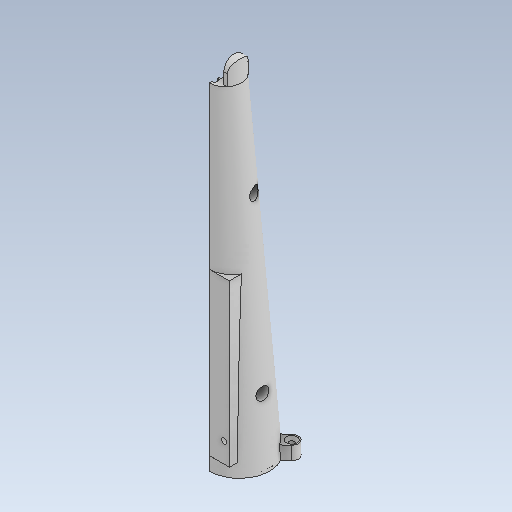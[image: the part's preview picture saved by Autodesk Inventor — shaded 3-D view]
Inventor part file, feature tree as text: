
AUTODESK INVENTOR PART (.ipt)
format: ipt  version: 2021 (Build 250183000, 183)  size: 1,106,432 bytes
history: native  units: mm
features: sketch x40, extrude x38, plane x17, fillet x9, hole x3, thread x3, loft x2, revolve x2, other x1
ambient origin geometry x8: Origin, YZ Plane, XZ Plane, XY Plane, X Axis, Y Axis, Z Axis, Center Point
bodies: Body1 (feature_tree)
feature tree (115):
  other  "Sólido1"
  plane  "Plano de trabajo1"
  plane  "Plano de trabajo2"
  plane  "Plano de trabajo4"
  plane  "Plano de trabajo5"
  plane  "Plano de trabajo6"
  sketch  "Boceto1"  dims[d1=250.0mm d2=0.0mm d3=-80.0mm d4=-110.0mm]
  sketch  "Boceto2"  dims[d5=-140.0mm d7=-0.0mm d8=2.0mm]
  sketch  "Boceto3"  dims[d9=140.0mm d10=250.0mm]
  sketch  "Boceto4"  dims[d11=24.0mm d22=0.0mm d23=90.0deg d24=0.0mm d25=90.0deg]
  sketch  "Boceto6"  dims[d44=45.0mm d49=29.11157mm]
  sketch  "Boceto7"  dims[d50=29.11157mm d53=29.11157mm]
  loft  "Solevación1"
  fillet  "Empalme2"  [1 undecoded]
  extrude  "Extrusión1"  TaperAngle=0.0deg  [1 undecoded]
  fillet  "Empalme5"  Radius=2.0mm
  plane  "Plano de trabajo7"
  extrude  "Extrusión2"  Depth=250.0mm
  plane  "Plano de trabajo8"
  plane  "Plano de trabajo9"
  loft  "Solevación9"
  plane  "Plano de trabajo10"
  extrude  "Extrusión3"  Depth=29.11157mm
  plane  "Plano de trabajo11"
  revolve  "Revolución1"  [1 undecoded]
  revolve  "Revolución2"  [1 undecoded]
  extrude  "Extrusión4"  Depth=32.5mm
  plane  "Plano de trabajo12"
  extrude  "Extrusión5"  Depth=44.747934mm
  plane  "Plano de trabajo13"
  plane  "Plano de trabajo14"
  extrude  "Extrusión6"  Depth=42.747934mm
  extrude  "Extrusión7"  Depth=42.747934mm
  extrude  "Extrusión8"  Depth=13.0mm
  extrude  "Extrusión11"  Depth=6.5mm
  extrude  "Extrusión9"  Depth=7.75mm
  extrude  "Extrusión10"  Depth=16.0mm
  extrude  "Extrusión12"  Depth=12.0mm
  sketch  "Boceto30"  dims[d160=-19.75mm d161=0.0mm]
  extrude  "Extrusión13"  Depth=7.75mm
  extrude  "Extrusión14"  Depth=6.5mm
  extrude  "Extrusión15"  TaperAngle=0.0deg  [1 undecoded]
  hole  "Agujero1"  [1 undecoded]
  thread  "Rosca1"  [1 undecoded]
  extrude  "Extrusión16"  Depth=2.0mm
  plane  "Plano de trabajo16"
  extrude  "Extrusión17"  TaperAngle=0.0deg  [1 undecoded]
  extrude  "Extrusión18"  TaperAngle=0.0deg  [1 undecoded]
  plane  "Plano de trabajo17"
  sketch  "Boceto46"  dims[d185=2.0mm d187=1.0mm]
  hole  "Agujero2"  [1 undecoded]
  hole  "Agujero3"  [1 undecoded]
  plane  "Plano de trabajo19"
  sketch  "Boceto50"  dims[d193=0.25mm d194=90.0deg]
  extrude  "Extrusión22"  Depth=12.0mm
  extrude  "Extrusión23"  [1 undecoded]
  extrude  "Extrusión24"  Depth=0.75mm
  plane  "Plano de trabajo20"
  extrude  "Extrusión25"  Depth=1.0mm
  fillet  "Empalme6"  Radius=11.0mm
  fillet  "Empalme7"  Radius=17.453293mm
  sketch  "Boceto49"  dims[d191=2.0mm d192=0.25mm]
  extrude  "Extrusión29"  Depth=0.75mm
  extrude  "Extrusión30"  Depth=0.25mm
  sketch  "Boceto44"  dims[d181=0.75mm d182=0.25mm]
  sketch  "Boceto47"  dims[d189=3.0mm d190=2.0mm]
  extrude  "Extrusión26"  Depth=0.25mm
  extrude  "Extrusión27"  Depth=2.0mm
  extrude  "Extrusión28"  Depth=2.0mm
  sketch  "Boceto45"  dims[d183=1.0mm d184=0.25mm]
  extrude  "Extrusión31"  Depth=2.0mm
  extrude  "Extrusión32"  TaperAngle=90.0deg  [1 undecoded]
  extrude  "Extrusión33"  [1 undecoded]
  extrude  "Extrusión34"  Depth=20.0mm
  extrude  "Extrusión35"  Depth=2.0mm
  thread  "Rosca2"  [1 undecoded]
  thread  "Rosca3"  [1 undecoded]
  fillet  "Empalme8"  [1 undecoded]
  fillet  "Empalme9"  Radius=0.5mm
  fillet  "Empalme10"  Radius=0.25mm
  fillet  "Empalme11"  [1 undecoded]
  extrude  "Extrusión36"  Depth=1.8mm TaperAngle=0.0deg
  extrude  "Extrusión37"  Depth=1.8mm TaperAngle=0.0deg
  fillet  "Empalme12"  Radius=2.0mm
  sketch  "Boceto54"  dims[d201=9.0mm d202=9.0mm d203=2.0mm d204=201.65mm d205=0.0mm d206=0.5mm d207=0.25mm d208=-7.5mm]
  extrude  "Agujero_tornillo_caja"  Depth=1.8mm
  extrude  "Extrusión40"  Depth=6.5mm
  extrude  "Test_section"  Depth=1.8mm
  extrude  "Extrusión41"  Depth=1.8mm
  sketch  "Boceto55"  dims[d209=100.0mm d210=0.0mm d211=35.0mm d212=0.0mm d213=210.0mm d214=0.0mm d215=2.0mm d216=1.059493mm d217=6.5mm d218=1.059493mm d219=5.0mm d220=2.0mm d221=0.0mm d222=2.0mm d223=6.5mm d224=1.059493mm d225=5.0mm d226=4.85mm d227=2.0mm d228=0.0mm d229=6.0mm d230=10.0mm d231=3.0mm d232=11.0mm d233=10.5mm d235=30.0deg d236=4.75mm d237=0.0mm d238=-17.0mm d239=100.0mm d240=0.0mm d241=6.5mm d242=1.65mm d243=3.3mm d244=15.6mm d245=2.0mm d247=16.0mm d248=2.0mm d249=0.0mm d250=4.5mm d251=0.75mm d252=2.5mm d253=1.0mm d254=11.0mm d255=17.453293mm d256=2.939597mm d257=0.75mm d258=0.75mm d259=0.25mm d260=1.0mm d261=0.25mm d262=2.0mm d263=1.0mm d264=3.0mm d265=2.0mm d266=2.0mm d267=0.25mm d268=0.25mm d269=40.0mm d270=1.0mm d271=1.0mm d272=7.75mm d273=0.5mm d274=8.5mm d275=90.0deg d276=0.0mm d277=17.75mm d280=22.5mm d281=2.0mm d282=0.0mm d283=0.0mm d292=2.0mm d293=0.0mm d296=3.5mm d297=0.0mm d299=4.0mm d300=3.708mm d301=3.023mm d302=2.0mm d303=14.3117mm d304=16.0mm d305=0.0mm d306=16.0mm d307=0.0mm d314=6.0mm d315=19.2mm d316=6.0mm d317=19.2mm d318=13.0mm d320=6.0mm d321=19.2mm d322=13.0mm d323=6.0mm d324=19.2mm d325=13.0mm d326=7.0mm d332=10.0mm d333=0.0mm d335=-41.6mm d336=4.0mm d337=1.0mm d338=9.0mm d339=4.0mm d340=1.0mm d341=9.0mm d342=4.0mm d343=5.2mm d344=6.0mm d345=0.0mm d346=15.0mm d347=5.0mm d349=5.0mm d351=0.0mm d352=45.0mm d354=10.0mm d355=10.0mm d356=0.0mm d357=15.0mm d358=0.0mm d359=2.0mm d363=50.4125mm d376=14.059493mm d377=2.0mm d378=0.0mm d379=2.0mm d380=11.25mm d381=90.0mm d382=290.0mm d383=14.059493mm d384=100.825mm d390=30.940507mm d391=2.0mm d392=100.825mm d393=14.790546mm d394=2.0mm d395=3.0mm d396=6.0mm d397=4.0mm d398=4.0mm d399=4.0mm d400=8.128453mm d401=12.0mm d402=4.45mm d403=2.5mm d404=1.65mm d405=1.65mm d406=1.0mm d407=2.0mm d408=2.0mm d409=0.0mm d411=50.4125mm d412=6.0mm d418=13.059493mm d419=6.5mm d420=6.5mm d421=50.4125mm d422=126.03125mm d423=0.0mm d424=15.0mm d425=5.0mm d426=5.0mm d427=0.0mm d428=45.0mm d429=10.0mm d430=2.0mm d431=4.0mm d432=6.0mm d433=8.0mm d434=2.0mm d435=90.0deg d436=20.0mm d437=0.0mm d438=4.0mm d439=6.0mm d440=8.0mm d441=2.0mm d442=90.0deg d443=20.0mm d444=0.0mm d446=10.0mm d447=3.0mm d448=11.0mm d450=9.2mm d451=9.2mm d452=90.0mm d453=750.0mm d454=22.5mm d455=43.0mm d456=44.0mm d457=14.059493mm d458=11.25mm d461=22.5mm d462=43.0mm d463=7.059493mm d464=3.0mm d465=6.0mm d466=3.0mm d467=6.0mm d468=45.0mm d469=130.0mm d470=17.04mm d471=30.0mm d472=15.0mm d473=0.0mm d474=1.5mm d475=2.0mm d476=1.5mm d477=2.0mm d478=120.0mm d479=0.0mm d480=120.0mm d481=0.0mm d482=116.0mm d483=0.0mm d484=69.0mm d485=0.0mm d486=-1.5mm d487=65.395511mm d488=2.6mm d489=60.0deg d490=45.0deg d491=15.0mm d492=1.6mm d493=0.0mm d494=180.0mm d495=0.0mm d496=180.0mm d497=0.0mm d498=2.0mm d499=0.0mm d500=4.1mm d501=4.4mm d502=10.0mm d503=0.0mm d504=7.0mm d505=0.0mm d506=7.0mm d507=0.0mm d508=4.4mm d509=4.4mm d510=4.4mm d511=7.0mm d512=0.0mm d513=25.497mm d514=0.0mm d515=0.0mm d516=0.0mm d517=4.0mm d518=4.0mm d519=2.0mm d520=0.0mm d521=2.0mm d522=0.0mm d523=2.0mm d524=0.0mm d525=1.0mm d526=0.8mm d527=1.0mm d528=0.8mm d533=3.0mm d534=1.5mm d537=1.0mm d538=6.5mm d539=3.0mm d540=1.5mm d541=0.0mm d542=0.0mm d543=2.0mm d544=0.0mm d545=2.5mm d546=135.0mm d547=4.0mm d548=130.0mm d549=0.0mm d550=0.0mm d551=25.0mm d552=11.0mm d553=4.0mm d554=6.0mm d555=12.0mm d556=0.0mm d557=10.0mm d558=0.0mm d559=1.2mm d560=1.8mm d561=0.0mm]
  sketch  "Boceto9"  dims[d59=29.11157mm d61=29.11157mm]
  sketch  "Boceto10"  dims[d65=22.5mm d66=32.5mm]
  sketch  "Boceto15"  dims[d67=22.5mm d90=44.747934mm]
  sketch  "Boceto16"  dims[d91=42.747934mm d93=42.747934mm]
  sketch  "Boceto17"  dims[d96=0.0mm d97=90.0deg d98=0.0mm d99=90.0deg d100=0.0mm d101=90.0deg d102=0.0mm d103=90.0deg d112=42.747934mm]
  sketch  "Boceto18"  dims[d115=5.0mm d120=13.0mm]
  sketch  "Boceto19"  dims[d121=6.5mm d124=7.75mm]
  sketch  "Boceto20"  dims[d125=7.75mm d126=7.75mm]
  sketch  "Boceto21"  dims[d127=7.75mm d130=16.0mm]
  sketch  "Boceto22"  dims[d131=0.0mm d132=12.0mm]
  sketch  "Boceto24"  dims[d133=12.0mm d134=7.75mm]
  sketch  "Boceto25"  dims[d135=6.5mm d136=7.75mm]
  sketch  "Boceto26"  dims[d137=15.0mm d138=0.0mm]
  sketch  "Boceto27"  dims[d146=-8.5mm d147=30.0mm d148=2.0mm]
  sketch  "Boceto28"  dims[d149=25.12mm d150=2.0mm]
  sketch  "Boceto29"  dims[d151=10.357mm d156=0.0mm d157=90.0deg d158=0.0mm d159=90.0deg]
  sketch  "Boceto31"  dims[d163=0.0mm d164=2.0mm]
  sketch  "Boceto36"  dims[d165=15.0mm d166=4.0mm]
  sketch  "Boceto37"  dims[d167=30.0mm d168=12.0mm]
  sketch  "Boceto38"  dims[d169=0.0mm d170=-7.25mm]
  sketch  "Boceto39"  dims[d171=4.5mm d172=0.75mm]
  sketch  "Boceto40"  dims[d173=2.5mm d174=1.0mm d176=11.0mm d177=17.453293mm]
  sketch  "Boceto41"  dims[d179=2.939597mm d180=0.75mm]
  sketch  "Boceto51"  dims[d196=4.381635mm d197=0.0mm d198=-48.35mm]
  sketch  "Boceto53"  dims[d199=12.0mm d200=20.0mm]
note: 18 required parameter values undecoded (feature->parameter linkage not recoverable at this tier; creation-order binding heuristic only, values carry confidence <= 0.55)